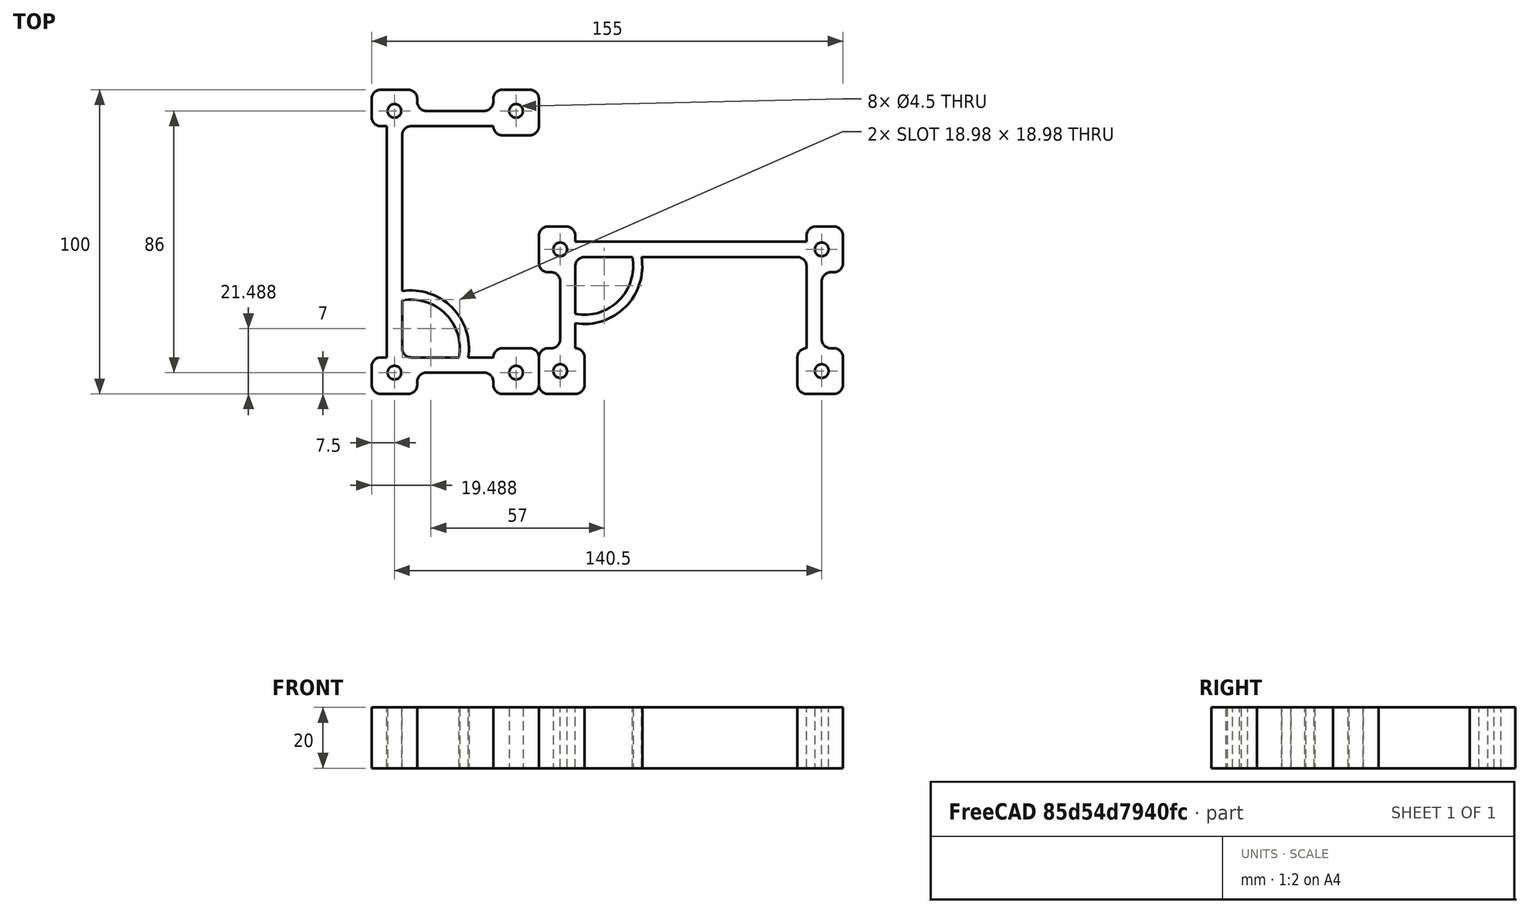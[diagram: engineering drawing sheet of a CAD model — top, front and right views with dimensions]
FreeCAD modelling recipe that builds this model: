
FCSTD DOCUMENT  (FreeCAD 0.15R4527 (Git))
Label: y_tower_space_param
License: All rights reserved
LicenseURL: http://en.wikipedia.org/wiki/All_rights_reserved
objects: Part::Feature×2, Mesh::Feature×1, Sketcher::SketchObject×1, PartDesign::Pad×1
note: 5 computed .brp shape members not serialized (recipe doc carries the construction recipe); baked Part::Feature solids carry a one-line shape summary decoded from their .brp

FEATURE [Mesh::Feature] towerspacer_10mm_must_be_same_dimension_as_table
FEATURE [Part::Feature] towerspacer_10mm_must_be_same_dimension_as_table001001  label="towerspacer_10mm_must_be_same_dimension_as_table002"
  shape: bbox 100 x 55 x 10 mm, 1331 faces, 0 solids (baked)
FEATURE [Sketcher::SketchObject] Sketch
  ExternalGeometry = -> [towerspacer_10mm_must_be_same_dimension_as_table001001]
  Placement = pos=(0,0,10) rot=(0,0,1;0rad)
  Support = -> towerspacer_10mm_must_be_same_dimension_as_table001001 [Face1331]
  sketch-geometry (52):
    g0: LineSegment StartX=33.7617 StartY=45 StartZ=0 EndX=85 EndY=45 EndZ=0
    g1: LineSegment StartX=33.7617 StartY=45 StartZ=0 EndX=85 EndY=45 EndZ=0
    g2: LineSegment StartX=88 StartY=42 StartZ=0 EndX=88 EndY=15 EndZ=0
    g3: LineSegment StartX=85 StartY=12 StartZ=0 EndX=85 EndY=3 EndZ=0
    g4: LineSegment StartX=88 StartY=-1e-12 StartZ=0 EndX=97 EndY=-1e-12 EndZ=0
    g5: LineSegment StartX=100 StartY=3 StartZ=0 EndX=100 EndY=12 EndZ=0
    g6: LineSegment StartX=96 StartY=15 StartZ=0 EndX=97 EndY=15 EndZ=0
    g7: LineSegment StartX=93 StartY=18 StartZ=0 EndX=93 EndY=37 EndZ=0
    g8: LineSegment StartX=96 StartY=40 StartZ=0 EndX=97 EndY=40 EndZ=0
    g9: LineSegment StartX=100 StartY=43 StartZ=0 EndX=100 EndY=52 EndZ=0
    g10: LineSegment StartX=97 StartY=55 StartZ=0 EndX=91 EndY=55 EndZ=0
    g11: LineSegment StartX=88 StartY=50 StartZ=0 EndX=12 EndY=50 EndZ=0
    g12: LineSegment StartX=88 StartY=50 StartZ=0 EndX=88 EndY=52 EndZ=0
    g13: LineSegment StartX=12 StartY=52 StartZ=0 EndX=12 EndY=50 EndZ=0
    g14: LineSegment StartX=9 StartY=55 StartZ=0 EndX=3 EndY=55 EndZ=0
    g15: LineSegment StartX=0 StartY=52 StartZ=0 EndX=0 EndY=43 EndZ=0
    g16: LineSegment StartX=3 StartY=40 StartZ=0 EndX=4 EndY=40 EndZ=0
    g17: LineSegment StartX=7 StartY=37 StartZ=0 EndX=7 EndY=18 EndZ=0
    g18: LineSegment StartX=4 StartY=15 StartZ=0 EndX=3 EndY=15 EndZ=0
    g19: LineSegment StartX=0 StartY=12 StartZ=0 EndX=4.5e-11 EndY=3 EndZ=0
    g20: LineSegment StartX=3 StartY=4.4e-11 StartZ=0 EndX=12 EndY=0 EndZ=0
    g21: LineSegment StartX=15 StartY=3 StartZ=0 EndX=15 EndY=12 EndZ=0
    g22: LineSegment StartX=12 StartY=15 StartZ=0 EndX=12 EndY=23.2383 EndZ=0
    g23: ArcOfCircle CenterX=15 CenterY=42 CenterZ=0 NormalX=0 NormalY=0 NormalZ=1 Radius=19 StartAngle=4.55383 EndAngle=6.44174
    g24: ArcOfCircle CenterX=9.00001 CenterY=52 CenterZ=0 NormalX=0 NormalY=0 NormalZ=1 Radius=2.99999 StartAngle=6.28318 EndAngle=7.85398
    g25: ArcOfCircle CenterX=2.99999 CenterY=52 CenterZ=0 NormalX=0 NormalY=0 NormalZ=1 Radius=2.99999 StartAngle=1.57079 EndAngle=3.1416
    g26: ArcOfCircle CenterX=3 CenterY=43 CenterZ=0 NormalX=0 NormalY=0 NormalZ=1 Radius=3 StartAngle=3.14159 EndAngle=4.71239
    g27: ArcOfCircle CenterX=4 CenterY=37 CenterZ=0 NormalX=0 NormalY=0 NormalZ=1 Radius=3 StartAngle=1.34771e-06 EndAngle=1.57079
    g28: ArcOfCircle CenterX=4 CenterY=18 CenterZ=0 NormalX=0 NormalY=0 NormalZ=1 Radius=3 StartAngle=4.71239 EndAngle=6.28318
    g29: ArcOfCircle CenterX=3 CenterY=12 CenterZ=0 NormalX=0 NormalY=0 NormalZ=1 Radius=3 StartAngle=1.5708 EndAngle=3.14159
    g30: ArcOfCircle CenterX=3 CenterY=3 CenterZ=0 NormalX=0 NormalY=0 NormalZ=1 Radius=3 StartAngle=3.14159 EndAngle=4.71239
    g31: ArcOfCircle CenterX=12 CenterY=3 CenterZ=0 NormalX=0 NormalY=0 NormalZ=1 Radius=3 StartAngle=4.71239 EndAngle=6.28318
    g32: ArcOfCircle CenterX=12 CenterY=12 CenterZ=0 NormalX=0 NormalY=0 NormalZ=1 Radius=3 StartAngle=1.61148e-06 EndAngle=1.57079
    g33: ArcOfCircle CenterX=85 CenterY=42 CenterZ=0 NormalX=0 NormalY=0 NormalZ=1 Radius=3 StartAngle=6.28318 EndAngle=7.85398
    g34: ArcOfCircle CenterX=88 CenterY=12 CenterZ=0 NormalX=0 NormalY=0 NormalZ=1 Radius=3 StartAngle=1.5708 EndAngle=3.14159
    g35: ArcOfCircle CenterX=88 CenterY=3 CenterZ=0 NormalX=0 NormalY=0 NormalZ=1 Radius=3 StartAngle=3.14159 EndAngle=4.71239
    g36: ArcOfCircle CenterX=97 CenterY=3 CenterZ=0 NormalX=0 NormalY=0 NormalZ=1 Radius=3 StartAngle=4.71239 EndAngle=6.28319
    g37: ArcOfCircle CenterX=97 CenterY=12 CenterZ=0 NormalX=0 NormalY=0 NormalZ=1 Radius=3 StartAngle=6.28318 EndAngle=7.85398
    g38: ArcOfCircle CenterX=96 CenterY=18 CenterZ=0 NormalX=0 NormalY=0 NormalZ=1 Radius=3 StartAngle=3.14159 EndAngle=4.71239
    g39: ArcOfCircle CenterX=96 CenterY=37 CenterZ=0 NormalX=0 NormalY=0 NormalZ=1 Radius=3 StartAngle=1.5708 EndAngle=3.14159
    g40: ArcOfCircle CenterX=97 CenterY=43 CenterZ=0 NormalX=0 NormalY=0 NormalZ=1 Radius=3 StartAngle=4.71239 EndAngle=6.28319
    g41: ArcOfCircle CenterX=97 CenterY=52 CenterZ=0 NormalX=0 NormalY=0 NormalZ=1 Radius=3 StartAngle=6.28318 EndAngle=7.85398
    g42: ArcOfCircle CenterX=91 CenterY=52 CenterZ=0 NormalX=0 NormalY=0 NormalZ=1 Radius=3 StartAngle=1.5708 EndAngle=3.14159
    g43: LineSegment StartX=33.7617 StartY=45 StartZ=0 EndX=85 EndY=45 EndZ=0
    g44: ArcOfCircle CenterX=15 CenterY=42 CenterZ=0 NormalX=0 NormalY=0 NormalZ=1 Radius=3 StartAngle=1.5708 EndAngle=3.14159
    g45: ArcOfCircle CenterX=15 CenterY=42 CenterZ=0 NormalX=0 NormalY=0 NormalZ=1 Radius=16 StartAngle=4.52377 EndAngle=6.4718
    g46: LineSegment StartX=15 StartY=45 StartZ=0 EndX=30.7162 EndY=45 EndZ=0
    g47: LineSegment StartX=12 StartY=42 StartZ=0 EndX=12 EndY=26.2838 EndZ=0
    g48: Circle CenterX=7 CenterY=47.5 CenterZ=0 NormalX=0 NormalY=0 NormalZ=1 Radius=2.25
    g49: Circle CenterX=7 CenterY=7.5 CenterZ=0 NormalX=0 NormalY=0 NormalZ=1 Radius=2.25
    g50: Circle CenterX=93 CenterY=7.5 CenterZ=0 NormalX=0 NormalY=0 NormalZ=1 Radius=2.25
    g51: Circle CenterX=93 CenterY=47.5 CenterZ=0 NormalX=0 NormalY=0 NormalZ=1 Radius=2.25
  constraints (130):
    c: Coincident(g0,g-4)
    c: Coincident(g0,g-4)
    c: Coincident(g1,g0)
    c: Coincident(g1,g0)
    c: Coincident(g2,g-13)
    c: Coincident(g2,g-13)
    c: Coincident(g3,g-14)
    c: Coincident(g3,g-14)
    c: Coincident(g4,g-15)
    c: Coincident(g4,g-15)
    c: Coincident(g5,g-16)
    c: Coincident(g5,g-16)
    c: Coincident(g6,g-22)
    c: Coincident(g6,g-22)
    c: Coincident(g7,g-12)
    c: Coincident(g7,g-12)
    c: Coincident(g8,g-23)
    c: Coincident(g8,g-23)
    c: Coincident(g9,g-11)
    c: Coincident(g9,g-11)
    c: Coincident(g10,g-10)
    c: Coincident(g10,g-10)
    c: Coincident(g11,g-3)
    c: Coincident(g11,g-18)
    c: Coincident(g12,g11)
    c: Coincident(g12,g-58)
    c: Coincident(g13,g-18)
    c: Coincident(g13,g11)
    c: Coincident(g14,g-17)
    c: Coincident(g14,g-17)
    c: Coincident(g15,g-19)
    c: Coincident(g15,g-19)
    c: Coincident(g16,g-20)
    c: Coincident(g16,g-20)
    c: Coincident(g17,g-6)
    c: Coincident(g17,g-6)
    c: Coincident(g18,g-21)
    c: Coincident(g18,g-21)
    c: Coincident(g19,g-8)
    c: Coincident(g19,g-8)
    c: Coincident(g20,g-9)
    c: Coincident(g20,g-9)
    c: Coincident(g21,g-7)
    c: Coincident(g21,g-7)
    c: Coincident(g22,g-5)
    c: Coincident(g22,g-5)
    c: Coincident(g23,g0)
    c: Coincident(g23,g22)
    c: PointOnObject(g-33,g23)
    c: Coincident(g24,g13)
    c: Coincident(g24,g14)
    c: PointOnObject(g-42,g24)
    c: Coincident(g25,g14)
    c: Coincident(g25,g15)
    c: PointOnObject(g-41,g25)
    c: Coincident(g26,g15)
    c: Coincident(g26,g16)
    c: PointOnObject(g-39,g26)
    c: Coincident(g27,g17)
    c: Coincident(g27,g16)
    c: PointOnObject(g-40,g27)
    c: Coincident(g28,g18)
    c: Coincident(g28,g17)
    c: PointOnObject(g-43,g28)
    c: Coincident(g29,g18)
    c: Coincident(g29,g19)
    c: PointOnObject(g-44,g29)
    c: Coincident(g30,g19)
    c: Coincident(g30,g20)
    c: PointOnObject(g-45,g30)
    c: Coincident(g31,g20)
    c: Coincident(g31,g21)
    c: PointOnObject(g-46,g31)
    c: Coincident(g32,g22)
    c: Coincident(g32,g21)
    c: PointOnObject(g-47,g32)
    c: Coincident(g33,g0)
    c: Coincident(g33,g2)
    c: PointOnObject(g-57,g33)
    c: Coincident(g34,g2)
    c: Coincident(g34,g3)
    c: PointOnObject(g-48,g34)
    c: Coincident(g35,g3)
    c: Coincident(g35,g4)
    c: Coincident(g36,g5)
    c: Coincident(g36,g4)
    c: PointOnObject(g-51,g36)
    c: Coincident(g37,g5)
    c: Coincident(g37,g6)
    c: PointOnObject(g-50,g37)
    c: Coincident(g38,g7)
    c: Coincident(g38,g6)
    c: PointOnObject(g-49,g38)
    c: Coincident(g39,g7)
    c: Coincident(g39,g8)
    c: PointOnObject(g-56,g39)
    c: Coincident(g40,g8)
    c: Coincident(g40,g9)
    c: PointOnObject(g-55,g40)
    c: Coincident(g41,g10)
    c: Coincident(g41,g9)
    c: PointOnObject(g-54,g41)
    c: Coincident(g42,g12)
    c: Coincident(g42,g10)
    c: PointOnObject(g-53,g42)
    c: PointOnObject(g-52,g35)
    c: Coincident(g43,g0)
    c: Coincident(g43,g0)
    c: Coincident(g44,g-59)
    c: Coincident(g44,g-60)
    c: PointOnObject(g-35,g44)
    c: Coincident(g45,g-59)
    c: Coincident(g45,g-60)
    c: PointOnObject(g-34,g45)
    c: Coincident(g46,g44)
    c: Coincident(g46,g45)
    c: Coincident(g47,g44)
    c: Coincident(g47,g45)
    c: PointOnObject(g-38,g48)
    c: PointOnObject(g-37,g48)
    c: PointOnObject(g-36,g48)
    c: PointOnObject(g-31,g49)
    c: PointOnObject(g-30,g49)
    c: PointOnObject(g-32,g49)
    c: PointOnObject(g-27,g50)
    c: PointOnObject(g-28,g50)
    c: PointOnObject(g-29,g50)
    c: PointOnObject(g-24,g51)
    c: PointOnObject(g-25,g51)
    c: PointOnObject(g-26,g51)
FEATURE [PartDesign::Pad] Pad  label="y_tower_space_param"
  Length = 20
  Length2 = 100
  Sketch = -> Sketch
  Type = 0
FEATURE [Part::Feature] Pad001  label="y_tower_space_param001"
  Placement = pos=(0,0,0) rot=(0,0,1;1.5708rad)
  shape: bbox 55 x 100 x 20 mm, 52 faces (baked)
